# Revit family: 49210USA_01
name_source: partatom
category: Plumbing Fixtures
units: mm (PartAtom-declared; Revit-internal decimal feet)

## family parameters
Always vertical = No
Cut with Voids When Loaded = No
OmniClass Number = 23.31.17.00
OmniClass Title = Showers
Part Type = Normal
Room Calculation Point = No
Round Connector Dimension = Use Diameter
Shared = No
Work Plane-Based = Yes

## types (1)
- Default - please load Revit Family Type Catalog
    Connector Description = Water Inlet 3/8
    Default Elevation = 48"
    Description = AXOR Citterio C Single lever bidet mixer with pop-up waste set
    Diameter = 1/2"
    Manufacturer = AXOR
    Material = AXOR - Metal - 001 Chrome
    Model = 49210USA
    Product Guid = 1e6209ab-7150-47a4-a5c2-f7a5ca6897c8
    Product Page URL = https://www.axor-design.com
    Product data url = https://bimobject.com
    URL = https://www.axor-design.com
    Version = 1

## geometry (parser evidence)
native form markers: Sweep x2
no freeform markers — native parametric forms only
